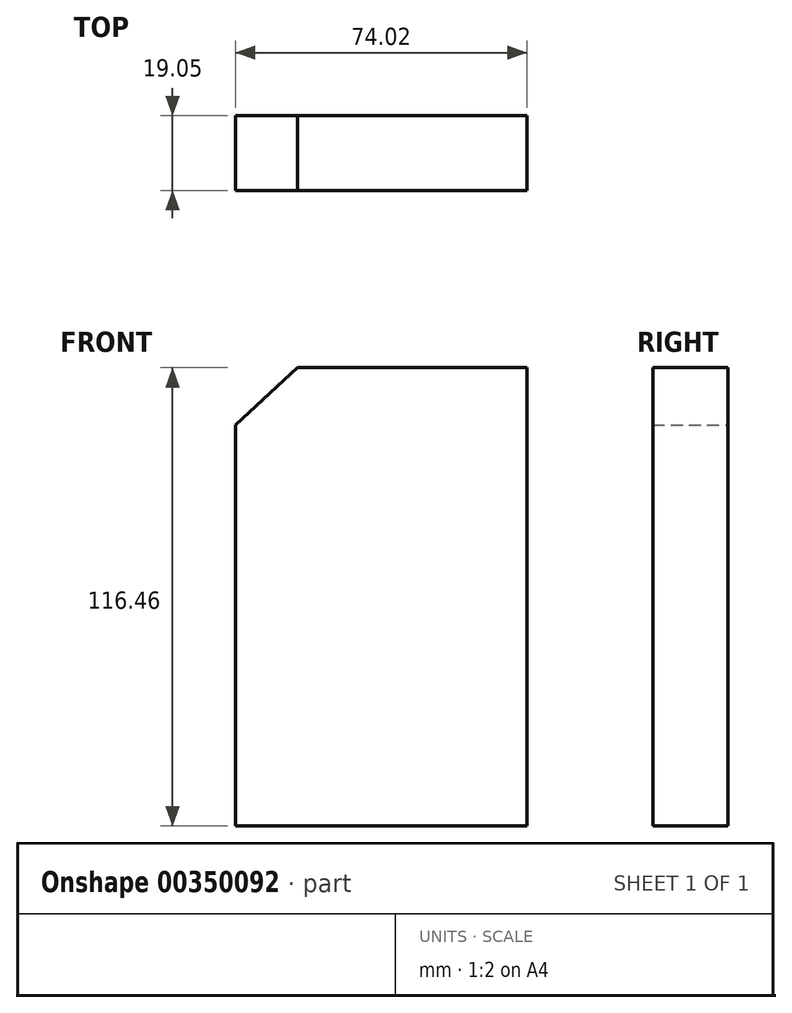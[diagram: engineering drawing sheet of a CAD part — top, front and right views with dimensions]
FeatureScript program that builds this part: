
annotation { "Feature Type Name" : "Feature", "Feature Type Description" : "" }
export const myFeature = defineFeature(function(context is Context, id is Id, definition is map)
    precondition{}
    {
        {
            var Q0;
            Q0=qCreatedBy(makeId("Front.planeOp"),FACE);
            var sketch = newSketch(context, id + "F0", { "sketchPlane" : qUnion([Q0])});
            skLineSegment(sketch, "E0.bottom", {"start": v(35.2, 56.23) * mm, "end": v(-23.15, 56.23) * mm});
            skLineSegment(sketch, "E0.top", {"start": v(35.2, -60.23) * mm, "end": v(-38.83, -60.23) * mm});
            skLineSegment(sketch, "E0.left", {"start": v(35.2, 56.23) * mm, "end": v(35.2, -60.23) * mm});
            skLineSegment(sketch, "E0.right", {"start": v(-38.83, 41.7) * mm, "end": v(-38.83, -60.23) * mm});
            skLineSegment(sketch, "E1", {"start": v(-38.83, 41.7) * mm, "end": v(-23.15, 56.23) * mm});
            skSolve(sketch);
        }
        {
            var Q0;
            Q0 = qSketchRegion(id + "F0", true);
            extrude(context, id + "F1", {"entities" : qUnion([Q0]), "depth" : 19.05 * mm});
        }
    });
